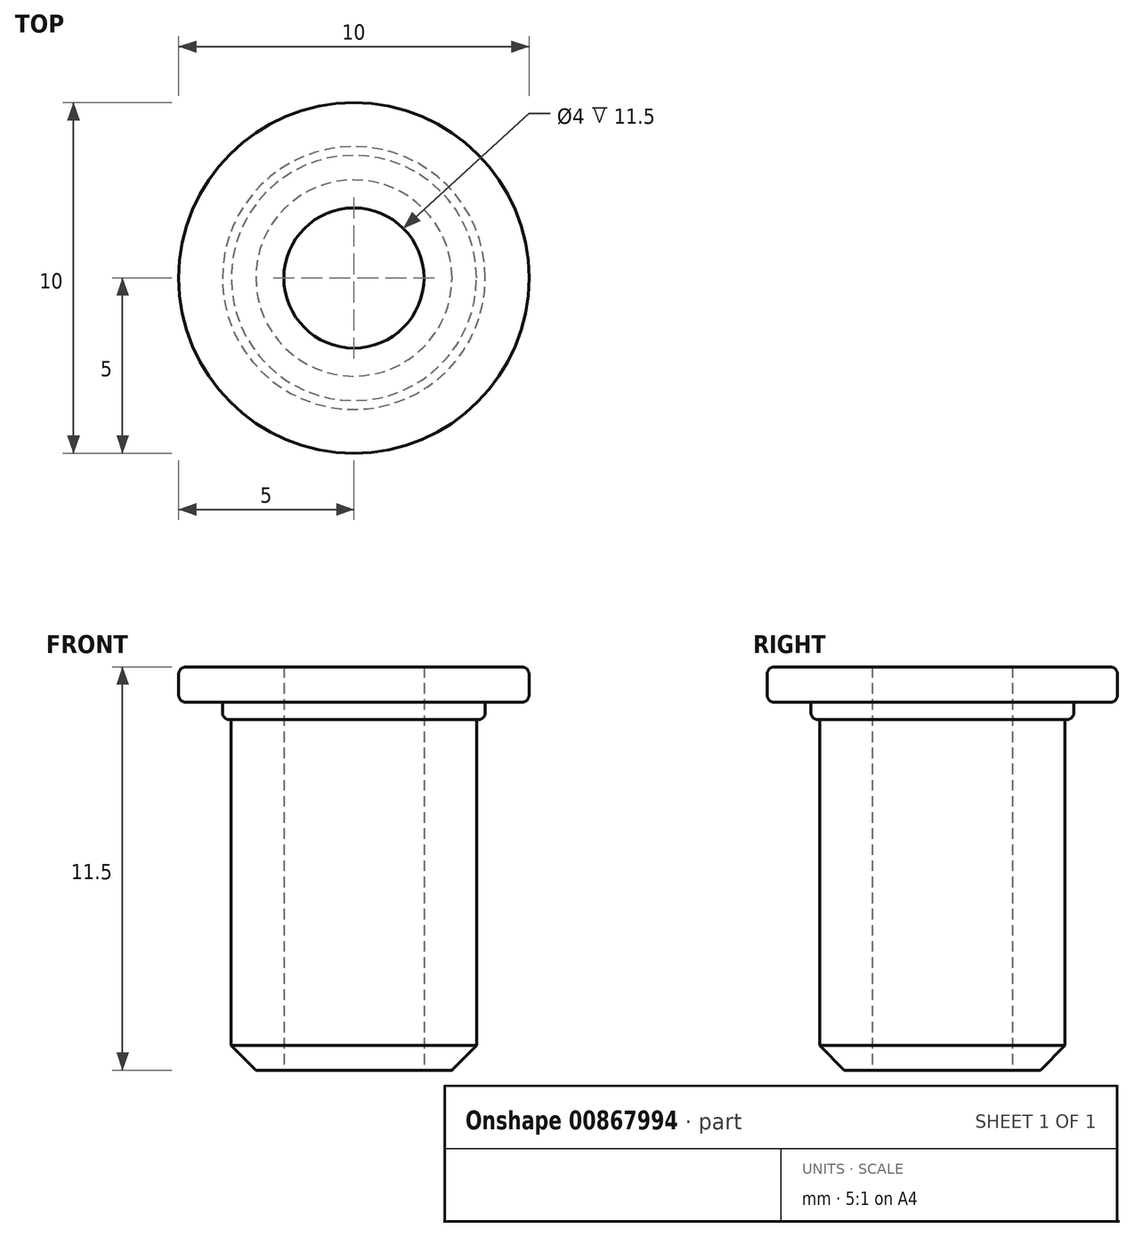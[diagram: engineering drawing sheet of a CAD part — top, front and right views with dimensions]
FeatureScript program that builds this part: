
annotation { "Feature Type Name" : "Feature", "Feature Type Description" : "" }
export const myFeature = defineFeature(function(context is Context, id is Id, definition is map)
    precondition{}
    {
        {
            var Q0;
            Q0=qCreatedBy(makeId("Top.planeOp"),FACE);
            var sketch = newSketch(context, id + "F0", { "sketchPlane" : qUnion([Q0])});
            skCircle(sketch, "E0", {"center": v(0, 0) * mm, "radius": 2 * mm});
            skCircle(sketch, "E1", {"center": v(0, 0) * mm, "radius": 3.5 * mm});
            skSolve(sketch);
        }
        {
            var Q0;
            Q0=makeQuery(id+"F0.imprint","IMPRINT",FACE,{"disambiguationData":[TD([[makeQuery(id+"F0.imprint","IMPRINT",EDGE,{"derivedFrom":sQuery(id+"F0.wireOp",EDGE,"E0")}),-1.0]])]});
            extrude(context, id + "F1", {"entities" : qUnion([Q0]), "depth" : 10 * mm, "offsetDistance" : 25 * mm});
        }
        {
            var Q0;
            Q0=makeQuery(id+"F1.opExtrude","CAP_FACE",FACE,{"disambiguationData":[OSD([sQuery(id+"F0.wireOp",EDGE,"E0"),sQuery(id+"F0.wireOp",EDGE,"E1")])],"isStart":false});
            var sketch = newSketch(context, id + "F2", { "sketchPlane" : qUnion([Q0])});
            skCircle(sketch, "E2", {"center": v(0, 0) * mm, "radius": 3.75 * mm});
            skCircle(sketch, "E3", {"center": v(0, 0) * mm, "radius": 2 * mm});
            skSolve(sketch);
        }
        {
            var Q0;
            Q0 = qSketchRegion(id + "F2", true);
            extrude(context, id + "F3", {"entities" : qUnion([Q0]), "operationType" : NewBodyOperationType.ADD, "depth" : 0.5 * mm, "offsetDistance" : 25 * mm});
        }
        {
            var Q0;
            Q0=makeQuery(id+"F3.opExtrude","CAP_FACE",FACE,{"disambiguationData":[OSD([sQuery(id+"F2.wireOp",EDGE,"E2"),sQuery(id+"F2.wireOp",EDGE,"E3")])],"isStart":false});
            var sketch = newSketch(context, id + "F4", { "sketchPlane" : qUnion([Q0])});
            skCircle(sketch, "E4", {"center": v(0, 0) * mm, "radius": 5 * mm});
            skCircle(sketch, "E5", {"center": v(0, 0) * mm, "radius": 2 * mm});
            skSolve(sketch);
        }
        {
            var Q0;
            Q0 = qSketchRegion(id + "F4", true);
            extrude(context, id + "F5", {"entities" : qUnion([Q0]), "operationType" : NewBodyOperationType.ADD, "depth" : 1 * mm, "offsetDistance" : 25 * mm});
        }
        {
            var Q0;
            Q0=makeQuery(id+"F5.opExtrude","CAP_EDGE",EDGE,{"disambiguationData":[OSD([sQuery(id+"F4.wireOp",EDGE,"E4")])],"isStart":true});
            var Q1;
            Q1=makeQuery(id+"F5.opExtrude","CAP_EDGE",EDGE,{"disambiguationData":[OSD([sQuery(id+"F4.wireOp",EDGE,"E4")])],"isStart":false});
            var Q2;
            Q2=makeQuery(id+"F3.opExtrude","CAP_EDGE",EDGE,{"disambiguationData":[OSD([sQuery(id+"F2.wireOp",EDGE,"E2")])],"isStart":true});
            fillet(context, id + "F6", {"entities" : qUnion([Q0, Q1, Q2]), "radius" : 0.2 * mm, "tangentPropagation" : true, "allowEdgeOverflow" : false});
        }
        {
            var Q0;
            Q0=makeQuery(id+"F1.opExtrude","CAP_EDGE",EDGE,{"disambiguationData":[OSD([sQuery(id+"F0.wireOp",EDGE,"E1")])],"isStart":true});
            chamfer(context, id + "F7", {"entities" : qUnion([Q0]), "width" : 0.7 * mm, "tangentPropagation" : true});
        }
    });
